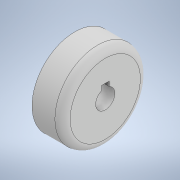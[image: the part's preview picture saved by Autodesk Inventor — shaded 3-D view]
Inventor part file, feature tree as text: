
AUTODESK INVENTOR PART (.ipt)
format: ipt  version: 2021.2 (Build 252289000, 289)  size: 132,608 bytes
history: native  units: in
note: dims shown in document units (in); Inventor stores cm internally (conversion verified against a paired STEP export)
features: sketch x2, revolve x1, extrude x1
ambient origin geometry x8: Origin, YZ Plane, XZ Plane, XY Plane, X Axis, Y Axis, Z Axis, Center Point
bodies: Solid1 (feature_tree)
feature tree (4):
  revolve  "Revolution1"  [1 undecoded]
  extrude  "Extrusion1"  Depth=0.125in
  sketch  "Sketch1"  dims[d0=0.7in d1=0.5in]
  sketch  "Sketch2"  dims[d2=0.1575in d3=0.125in d4=90.0deg d5=0.125in d6=0.125in d7=0.0in d8=0.0in]
note: 1 required parameter value undecoded (feature->parameter linkage not recoverable at this tier; creation-order binding heuristic only, values carry confidence <= 0.55)
